# Revit family: Midmark - Exam Table Adjustable Electric Column
name_source: partatom
category: Specialty Equipment
revit_build: Autodesk Revit 2017 (Build: 20190507_1515(x64)
units: mm (PartAtom-declared; Revit-internal decimal feet)

## family parameters
Always vertical = Yes
Cut with Voids When Loaded = No
OmniClass Number = 23.40.00.00
OmniClass Title = Equipment and Furnishings
Part Type = Normal
Room Calculation Point = No
Round Connector Dimension = Use Diameter
Shared = No
Work Plane-Based = No

## types (1)
- Standard Top w/ Foot Control
    Depth = 1' - 10"
    Electric Control Box Material = Stainless Steel, Polished
    Height = 3' - 0"
    Lift Column Material = Stainless Steel, Polished
    Lift Housing Material = Stainless Steel, Polished
    Manufacturer = MIDMARK
    Model = 101-8640-03
    Pedestal Base Depth = 1' - 6"
    Pedestal Base Width = 2' - 0"
    Platform Base Material = Stainless Steel, Polished
    Table Top Material = Stainless Steel, Polished
    Type Comments = Exam Table with Adjustable Electric Column, 44"L X 22"W Stainless Steel Top
    Weight = 0
    Width = 3' - 8"

## geometry (parser evidence)
native form markers: Sweep x2
no freeform markers — native parametric forms only
